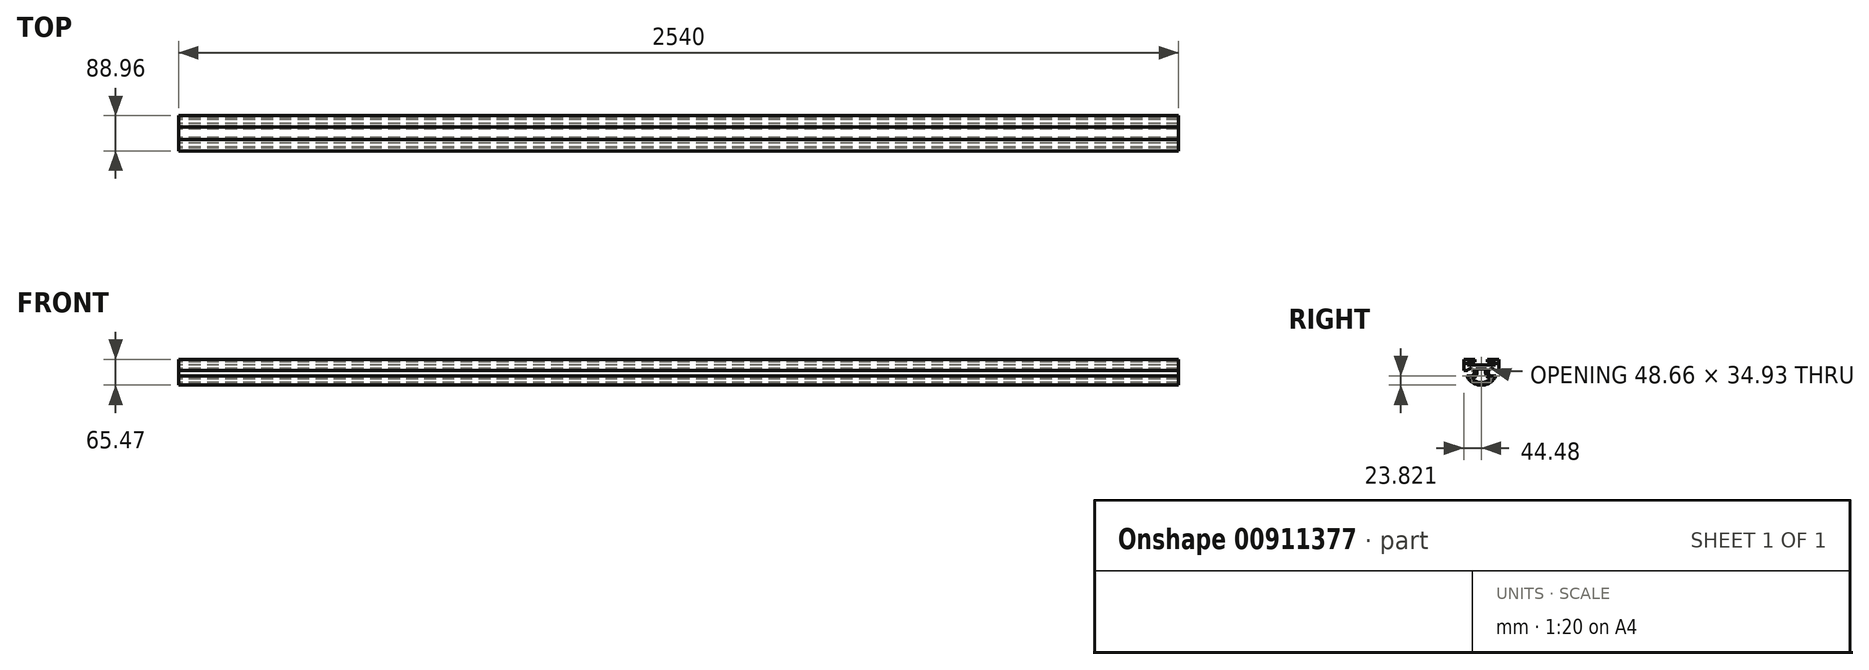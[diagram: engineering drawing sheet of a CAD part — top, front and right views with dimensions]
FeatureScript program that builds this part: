
annotation { "Feature Type Name" : "Feature", "Feature Type Description" : "" }
export const myFeature = defineFeature(function(context is Context, id is Id, definition is map)
    precondition{}
    {
        {
            var Q0;
            Q0=qCreatedBy(makeId("Right.planeOp"),FACE);
            var sketch = newSketch(context, id + "F0", { "sketchPlane" : qUnion([Q0])});
            skLineSegment(sketch, "E0", {"start": v(0, 55.17) * mm, "end": v(0, -40.1) * mm, "construction": true});
            skLineSegment(sketch, "E1", {"start": v(0, 10.69) * mm, "end": v(-35.3, 10.69) * mm});
            skLineSegment(sketch, "E2", {"start": v(-35.3, 10.69) * mm, "end": v(-35.3, 19.1) * mm});
            skLineSegment(sketch, "E3", {"start": v(-35.3, 19.1) * mm, "end": v(-15.87, 19.1) * mm});
            skLineSegment(sketch, "E4", {"start": v(-15.87, 19.1) * mm, "end": v(-15.87, 25.37) * mm});
            skLineSegment(sketch, "E5", {"start": v(-15.87, 25.37) * mm, "end": v(-44.48, 25.37) * mm});
            skLineSegment(sketch, "E6", {"start": v(-44.48, 25.37) * mm, "end": v(-44.48, -2.53) * mm});
            skLineSegment(sketch, "E7", {"start": v(-44.48, -2.53) * mm, "end": v(-35.16, -2.53) * mm});
            skArc(sketch, "E8", {"start": v(-27.31, -16.95) * mm, "mid": v(-19.05, -3.1) * mm, "end": v(-35.16, -2.53) * mm});
            skLineSegment(sketch, "E9", {"start": v(-27.31, -16.95) * mm, "end": v(-37.09, -16.95) * mm});
            skArc(sketch, "E10", {"start": v(-37.09, -16.95) * mm, "mid": v(-21.86, -33.84) * mm, "end": v(0, -40.1) * mm});
            skArc(sketch, "E11.0", {"start": v(-24.33, -23.88) * mm, "mid": v(-12.14, -14.28) * mm, "end": v(-13.33, 1.19) * mm});
            skLineSegment(sketch, "E12", {"start": v(-13.33, 1.19) * mm, "end": v(0, 1.19) * mm});
            skArc(sketch, "E13.0", {"start": v(-24.33, -23.88) * mm, "mid": v(-13.13, -31.19) * mm, "end": v(0, -33.75) * mm});
            skLineSegment(sketch, "E14.MirrorCS", {"start": v(27.31, -16.95) * mm, "end": v(37.09, -16.95) * mm});
            skLineSegment(sketch, "E15.MirrorCS", {"start": v(35.3, 10.69) * mm, "end": v(35.3, 19.1) * mm});
            skArc(sketch, "E16.MirrorCS", {"start": v(37.09, -16.95) * mm, "mid": v(21.86, -33.84) * mm, "end": v(0, -40.1) * mm});
            skArc(sketch, "E17.MirrorCS", {"start": v(24.33, -23.88) * mm, "mid": v(12.14, -14.28) * mm, "end": v(13.33, 1.19) * mm});
            skArc(sketch, "E18.MirrorCS", {"start": v(27.31, -16.95) * mm, "mid": v(19.05, -3.1) * mm, "end": v(35.16, -2.53) * mm});
            skArc(sketch, "E19.MirrorCS", {"start": v(24.33, -23.88) * mm, "mid": v(13.13, -31.19) * mm, "end": v(0, -33.75) * mm});
            skLineSegment(sketch, "E20.MirrorCS", {"start": v(15.87, 25.37) * mm, "end": v(44.48, 25.37) * mm});
            skLineSegment(sketch, "E21.MirrorCS", {"start": v(15.87, 19.1) * mm, "end": v(15.87, 25.37) * mm});
            skLineSegment(sketch, "E22.MirrorCS", {"start": v(44.48, -2.53) * mm, "end": v(35.16, -2.53) * mm});
            skLineSegment(sketch, "E23.MirrorCS", {"start": v(44.48, 25.37) * mm, "end": v(44.48, -2.53) * mm});
            skLineSegment(sketch, "E24.MirrorCS", {"start": v(0, 10.69) * mm, "end": v(35.3, 10.69) * mm});
            skLineSegment(sketch, "E25.MirrorCS", {"start": v(13.33, 1.19) * mm, "end": v(0, 1.19) * mm});
            skLineSegment(sketch, "E26.MirrorCS", {"start": v(35.3, 19.1) * mm, "end": v(15.87, 19.1) * mm});
            skSolve(sketch);
        }
        {
            var Q0;
            Q0=makeQuery(id+"F0.imprint","IMPRINT",FACE,{"disambiguationData":[TD([[makeQuery(id+"F0.imprint","IMPRINT",EDGE,{"derivedFrom":sQuery(id+"F0.wireOp",EDGE,"E1")}),1.0]])]});
            extrude(context, id + "F1", {"entities" : qUnion([Q0]), "endBound" : BoundingType.SYMMETRIC, "depth" : 2540 * mm, "offsetDistance" : 25.4 * mm});
        }
    });
